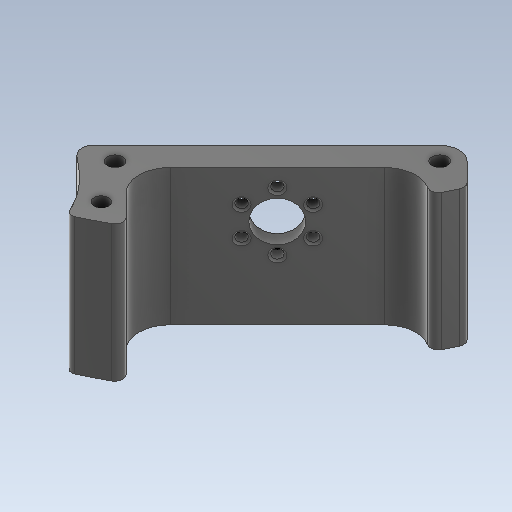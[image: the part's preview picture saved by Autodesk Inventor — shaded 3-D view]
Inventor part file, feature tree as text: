
AUTODESK INVENTOR PART (.ipt)
format: ipt  version: 2020 (Build 240168000, 168)  size: 688,128 bytes
history: native  units: mm
features: extrude x6, sketch x5, other x1, chamfer x1, fillet x1, projected_geometry x1
ambient origin geometry x8: Origin, YZ Plane, XZ Plane, XY Plane, X Axis, Y Axis, Z Axis, Center Point
bodies: Body1 (feature_tree)
feature tree (15):
  other  "Твердое тело1"
  sketch  "Эскиз1"
  extrude  "Выдавливание10"  Depth=4.0mm
  sketch  "Эскиз6"
  extrude  "Выдавливание13"  Depth=6.0mm
  extrude  "Выдавливание14"  Depth=35.0mm TaperAngle=0.0deg
  chamfer  "Фаска3"  Distance=59.0mm
  extrude  "Выдавливание15"  Depth=21.2mm
  fillet  "Сопряжение1"  Radius=15.0mm
  extrude  "Выдавливание16"  Depth=10.4mm
  extrude  "Выдавливание17"  Depth=2.5mm
  sketch  "Эскиз7"
  sketch  "Эскиз8"
  projected_geometry  "Спроецированная петля3"
  sketch  "Эскиз9"
